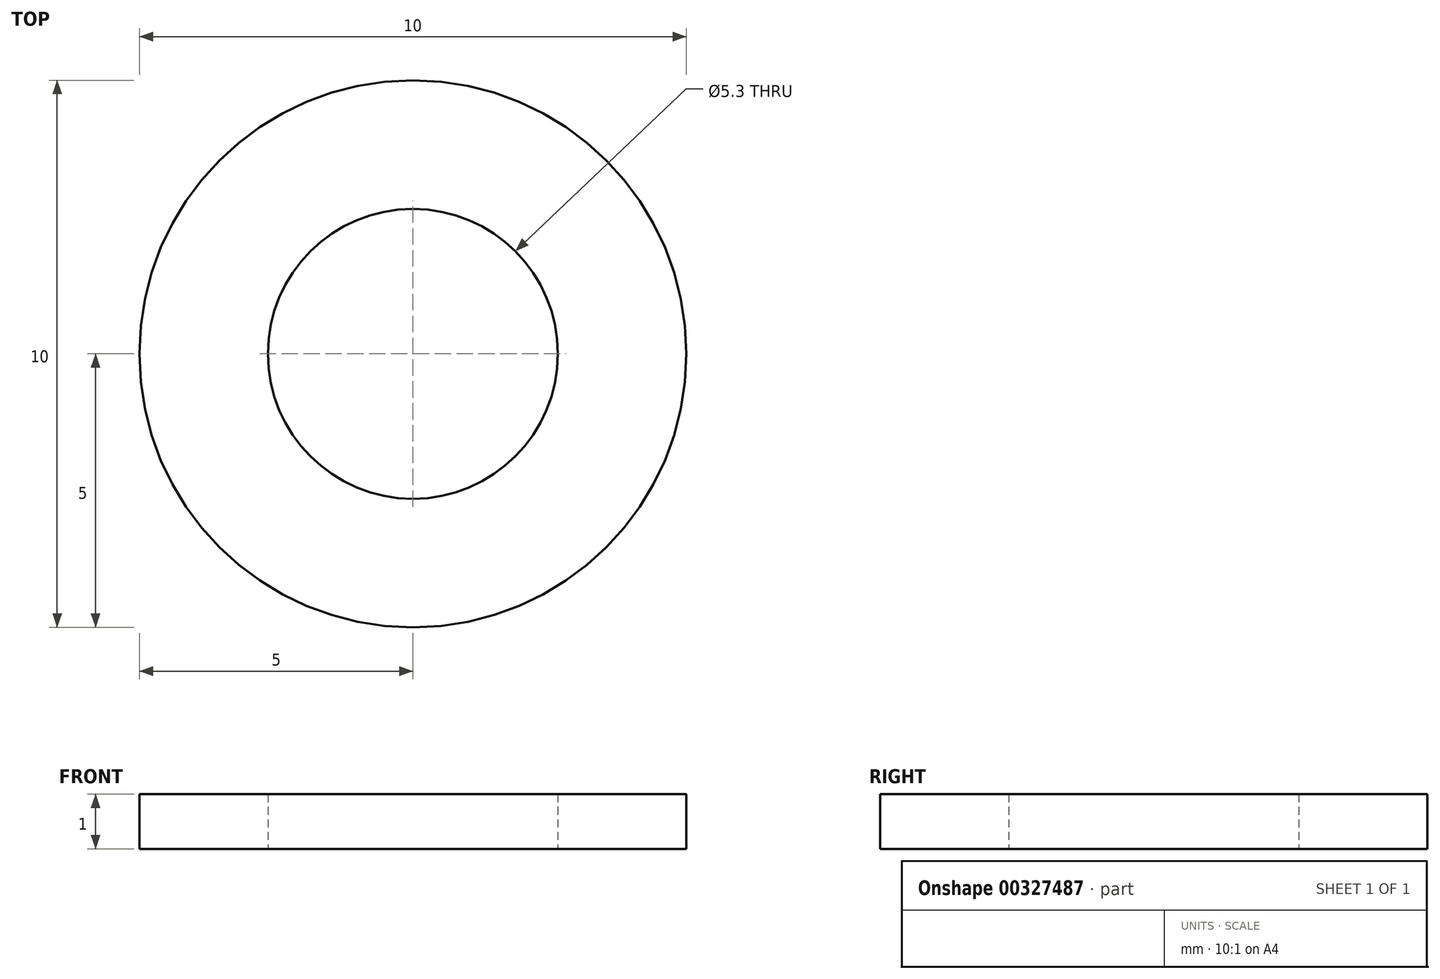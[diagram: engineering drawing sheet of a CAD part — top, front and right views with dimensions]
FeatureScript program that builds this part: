
annotation { "Feature Type Name" : "Feature", "Feature Type Description" : "" }
export const myFeature = defineFeature(function(context is Context, id is Id, definition is map)
    precondition{}
    {
        {
            var Q0;
            Q0=qCreatedBy(makeId("Top.planeOp"),FACE);
            var sketch = newSketch(context, id + "F0", { "sketchPlane" : qUnion([Q0])});
            skCircle(sketch, "E0", {"center": v(0, 0) * mm, "radius": 2.65 * mm});
            skCircle(sketch, "E1", {"center": v(0, 0) * mm, "radius": 5 * mm});
            skSolve(sketch);
        }
        {
            var Q0;
            Q0 = qSketchRegion(id + "F0", true);
            extrude(context, id + "F1", {"entities" : qUnion([Q0]), "depth" : 1 * mm});
        }
    });
